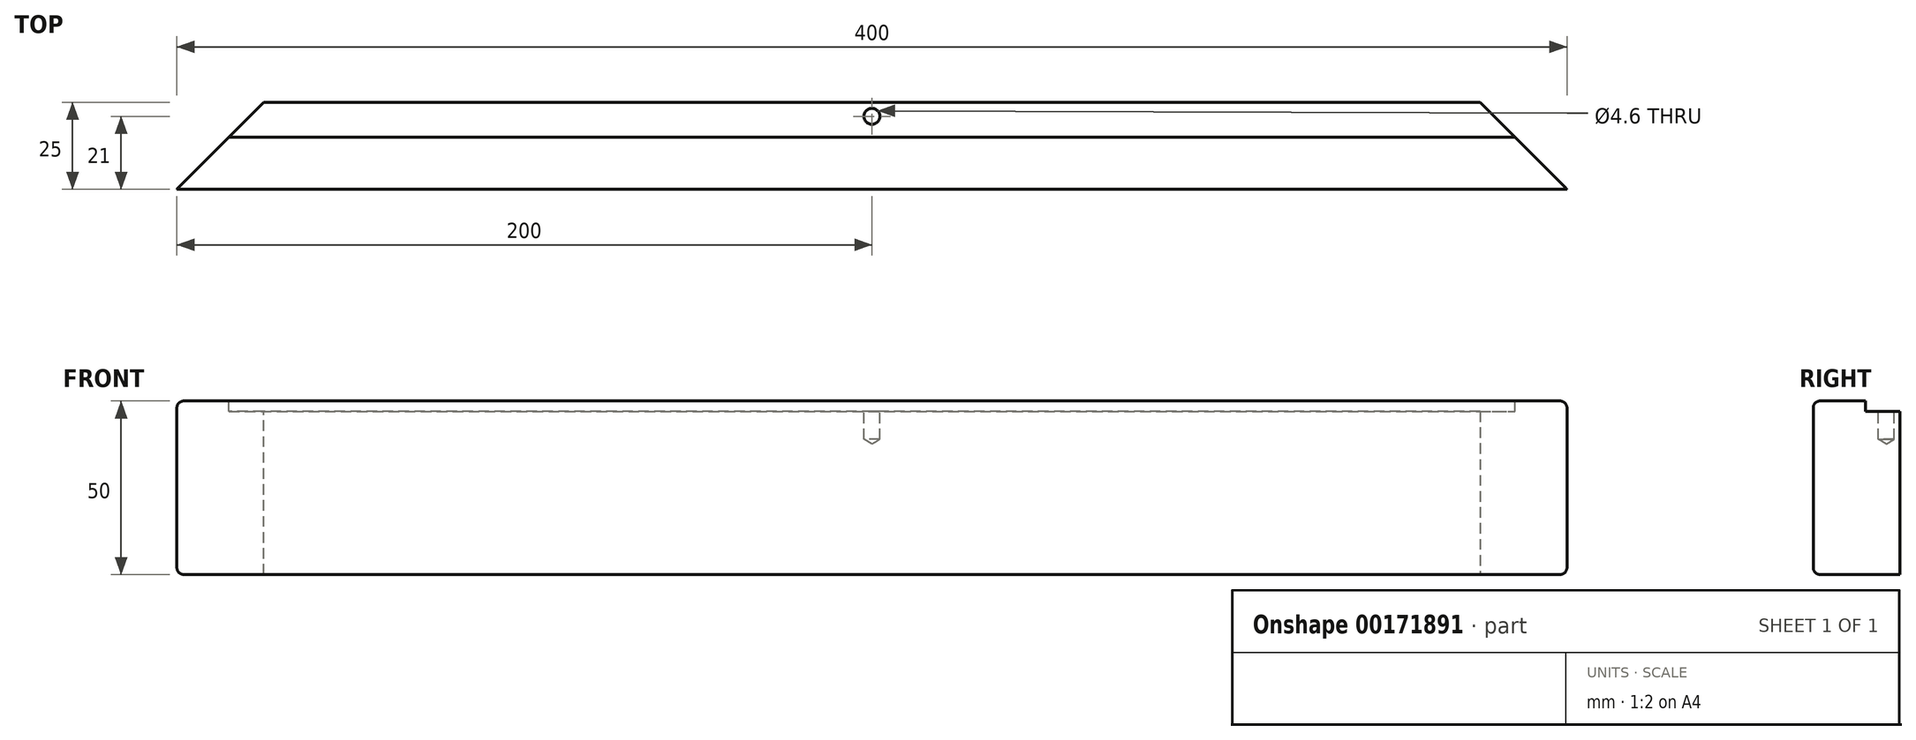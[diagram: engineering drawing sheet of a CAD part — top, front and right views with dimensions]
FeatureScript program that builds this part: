
annotation { "Feature Type Name" : "Feature", "Feature Type Description" : "" }
export const myFeature = defineFeature(function(context is Context, id is Id, definition is map)
    precondition{}
    {
        {
            var Q0;
            Q0=qCreatedBy(makeId("Front.planeOp"),FACE);
            var sketch = newSketch(context, id + "F0", { "sketchPlane" : qUnion([Q0])});
            skLineSegment(sketch, "E0.bottom", {"start": v(200, -25) * mm, "end": v(-200, -25) * mm});
            skLineSegment(sketch, "E0.top", {"start": v(200, 25) * mm, "end": v(-200, 25) * mm});
            skLineSegment(sketch, "E0.left", {"start": v(200, -25) * mm, "end": v(200, 25) * mm});
            skLineSegment(sketch, "E0.right", {"start": v(-200, -25) * mm, "end": v(-200, 25) * mm});
            skLineSegment(sketch, "E1", {"start": v(-200, 25) * mm, "end": v(200, -25) * mm, "construction": true});
            skLineSegment(sketch, "E2", {"start": v(200, 25) * mm, "end": v(-200, -25) * mm, "construction": true});
            skSolve(sketch);
        }
        {
            var Q0;
            Q0=makeQuery(id+"F0.imprint","IMPRINT",FACE,{"disambiguationData":[TD([[makeQuery(id+"F0.imprint","IMPRINT",EDGE,{"derivedFrom":sQuery(id+"F0.wireOp",EDGE,"E0.bottom")}),-1.0]])]});
            var Q1;
            Q1=makeQuery(id+"F0.imprint","IMPRINT",FACE,{"disambiguationData":[TD([[makeQuery(id+"F0.imprint","IMPRINT",EDGE,{"derivedFrom":sQuery(id+"F0.wireOp",EDGE,"TQ8CQex1-5ZuT-i06m-JSEl-Rafa6eQsYN91.left")}),1.0]])]});
            var Q2;
            Q2=makeQuery(id+"F0.imprint","IMPRINT",FACE,{"disambiguationData":[TD([[makeQuery(id+"F0.imprint","IMPRINT",EDGE,{"derivedFrom":sQuery(id+"F0.wireOp",EDGE,"XVRcOiwa-wmZa-OlfB-imAZ-ZysaIvfTFvSH")}),1.0]])]});
            var Q3;
            Q3=makeQuery(id+"F0.imprint","IMPRINT",FACE,{"disambiguationData":[TD([[makeQuery(id+"F0.imprint","IMPRINT",EDGE,{"derivedFrom":sQuery(id+"F0.wireOp",EDGE,"492701c9-3a02-475b-877f-e4fc534a5983")}),1.0]])]});
            var Q4;
            Q4=makeQuery(id+"F0.imprint","IMPRINT",FACE,{"disambiguationData":[TD([[makeQuery(id+"F0.imprint","IMPRINT",EDGE,{"derivedFrom":sQuery(id+"F0.wireOp",EDGE,"TQ8CQex1-5ZuT-i06m-JSEl-Rafa6eQsYN91.right")}),-1.0]])]});
            var Q5;
            {var subQ5=sQuery(id+"F0.wireOp",EDGE,"11b40b25-8dd5-4f7b-a4c1-55c3ff725173.left");Q5=makeQuery(id+"F0.imprint","IMPRINT",FACE,{"disambiguationData":[TD([[makeQuery(id+"F0.imprint","IMPRINT",EDGE,{"derivedFrom":subQ5}),1.0]])]});}
            var Q6;
            {var subQ0=sQuery(id+"F0.wireOp",EDGE,"050ddf37-6dd0-4eab-8f6c-0359ba11038c.filletArc");Q6=makeQuery(id+"F0.imprint","IMPRINT",FACE,{"disambiguationData":[TD([[makeQuery(id+"F0.imprint","IMPRINT",EDGE,{"derivedFrom":subQ0}),1.0]])]});}
            extrude(context, id + "F1", {"entities" : qUnion([Q0, Q1, Q2, Q3, Q4, Q5, Q6]), "depth" : 25 * mm});
        }
        {
            var Q0;
            Q0=makeQuery(id+"F1.opExtrude","CAP_EDGE",EDGE,{"disambiguationData":[OSD([sQuery(id+"F0.wireOp",EDGE,"E0.right")])],"isStart":true});
            var Q1;
            Q1=makeQuery(id+"F1.opExtrude","CAP_EDGE",EDGE,{"disambiguationData":[OSD([sQuery(id+"F0.wireOp",EDGE,"E0.left")])],"isStart":true});
            chamfer(context, id + "F2", {"entities" : qUnion([Q0, Q1]), "width" : 25 * mm, "tangentPropagation" : true});
        }
        {
            var Q0;
            Q0=makeQuery(id+"F1.opExtrude","SWEPT_FACE",FACE,{"disambiguationData":[OSD([sQuery(id+"F0.wireOp",EDGE,"E0.top")])]});
            var sketch = newSketch(context, id + "F3", { "sketchPlane" : qUnion([Q0])});
            skLineSegment(sketch, "E3", {"start": v(-185, -10) * mm, "end": v(185, -10) * mm});
            skLineSegment(sketch, "E4", {"start": v(-134.9, -4) * mm, "end": v(125.52, -4) * mm, "construction": true});
            skLineSegment(sketch, "E5", {"start": v(0, 10.75) * mm, "end": v(0, -16.45) * mm, "construction": true});
            skPoint(sketch, "E5.endSnap0", {"position": v(0, -10) * mm});
            skPoint(sketch, "E6", {"position": v(0, -4) * mm});
            skSolve(sketch);
        }
        {
            var Q0;
            {var subQ0=sQuery(id+"F3.wireOp",EDGE,"E3");Q0=makeQuery(id+"F3.imprint","IMPRINT",FACE,{"disambiguationData":[TD([[makeQuery(id+"F3.imprint","IMPRINT",EDGE,{"derivedFrom":subQ0}),1.0]])]});}
            extrude(context, id + "F4", {"entities" : qUnion([Q0]), "operationType" : NewBodyOperationType.REMOVE, "oppositeDirection" : true, "depth" : 3 * mm});
        }
        {
            var Q0;
            Q0=makeQuery(id+"F4.boolean.opBoolean","COPY",FACE,{"derivedFrom":makeQuery(id+"F4.opExtrude","CAP_FACE",FACE,{"disambiguationData":[OSD([sQuery(id+"F0.wireOp",EDGE,"E0.top"),sQuery(id+"F0.wireOp",EDGE,"E0.left"),sQuery(id+"F0.wireOp",EDGE,"E0.right"),sQuery(id+"F3.wireOp",EDGE,"E3")])],"isStart":false})});
            var sketch = newSketch(context, id + "F5", { "sketchPlane" : qUnion([Q0])});
            skLineSegment(sketch, "E7", {"start": v(-160.86, -4) * mm, "end": v(157.5, -4) * mm, "construction": true});
            skLineSegment(sketch, "E8", {"start": v(0, -19.46) * mm, "end": v(0, 5.76) * mm, "construction": true});
            skPoint(sketch, "E8.startSnap0", {"position": v(0, -10) * mm});
            skPoint(sketch, "E8.endSnap0", {"position": v(0, 0) * mm});
            skPoint(sketch, "E9", {"position": v(0, -4) * mm});
            skSolve(sketch);
        }
        {
            var Q0;
            Q0=sQuery(id+"F5.wireOp",VERTEX,"E9");
            var Q1;
            Q1=makeQuery(id+"F1.opExtrude","SWEPT_BODY",BODY,{"disambiguationData":[OSD([sQuery(id+"F0.wireOp",EDGE,"E0.bottom"),sQuery(id+"F0.wireOp",EDGE,"E0.top"),sQuery(id+"F0.wireOp",EDGE,"E0.left"),sQuery(id+"F0.wireOp",EDGE,"E0.right"),sQuery(id+"F0.wireOp",EDGE,"OmMS4I8q-v5Nw-sNs6-rLWv-C37PQFSncukl.bottom"),sQuery(id+"F0.wireOp",EDGE,"OmMS4I8q-v5Nw-sNs6-rLWv-C37PQFSncukl.top"),sQuery(id+"F0.wireOp",EDGE,"OmMS4I8q-v5Nw-sNs6-rLWv-C37PQFSncukl.left"),sQuery(id+"F0.wireOp",EDGE,"OmMS4I8q-v5Nw-sNs6-rLWv-C37PQFSncukl.right"),sQuery(id+"F0.wireOp",EDGE,"a599c4f8-9d5b-4f08-a6f5-21f0fa9e66a0.filletArc"),sQuery(id+"F0.wireOp",EDGE,"32fc2319-0cb2-45e8-9aa6-fcf55b2109a0.filletArc"),sQuery(id+"F0.wireOp",EDGE,"258bbff2-458d-4a09-ab05-362c01f2241a.filletArc"),sQuery(id+"F0.wireOp",EDGE,"b6ee52c4-7d80-4818-82dd-608125603be5.filletArc")])]});
            hole(context, id + "F6", {"style" : HoleStyle.SIMPLE, "endStyle" : HoleEndStyle.BLIND, "holeDiameter" : 4.6 * mm, "holeDepth" : 8 * mm, "startFromSketch" : true, "locations" : qUnion([Q0]), "scope" : qUnion([Q1])});
        }
        {
            var Q0;
            Q0=makeQuery(id+"F1.opExtrude","CAP_EDGE",EDGE,{"disambiguationData":[OSD([sQuery(id+"F0.wireOp",EDGE,"E0.top")])],"isStart":false});
            var Q1;
            Q1=makeQuery(id+"F1.opExtrude","CAP_EDGE",EDGE,{"disambiguationData":[OSD([sQuery(id+"F0.wireOp",EDGE,"E0.bottom")])],"isStart":false});
            fillet(context, id + "F7", {"entities" : qUnion([Q0, Q1]), "radius" : 2 * mm, "tangentPropagation" : true, "defaultsChanged" : false, "vertexSettings" : [], "allowEdgeOverflow" : false});
        }
    });
